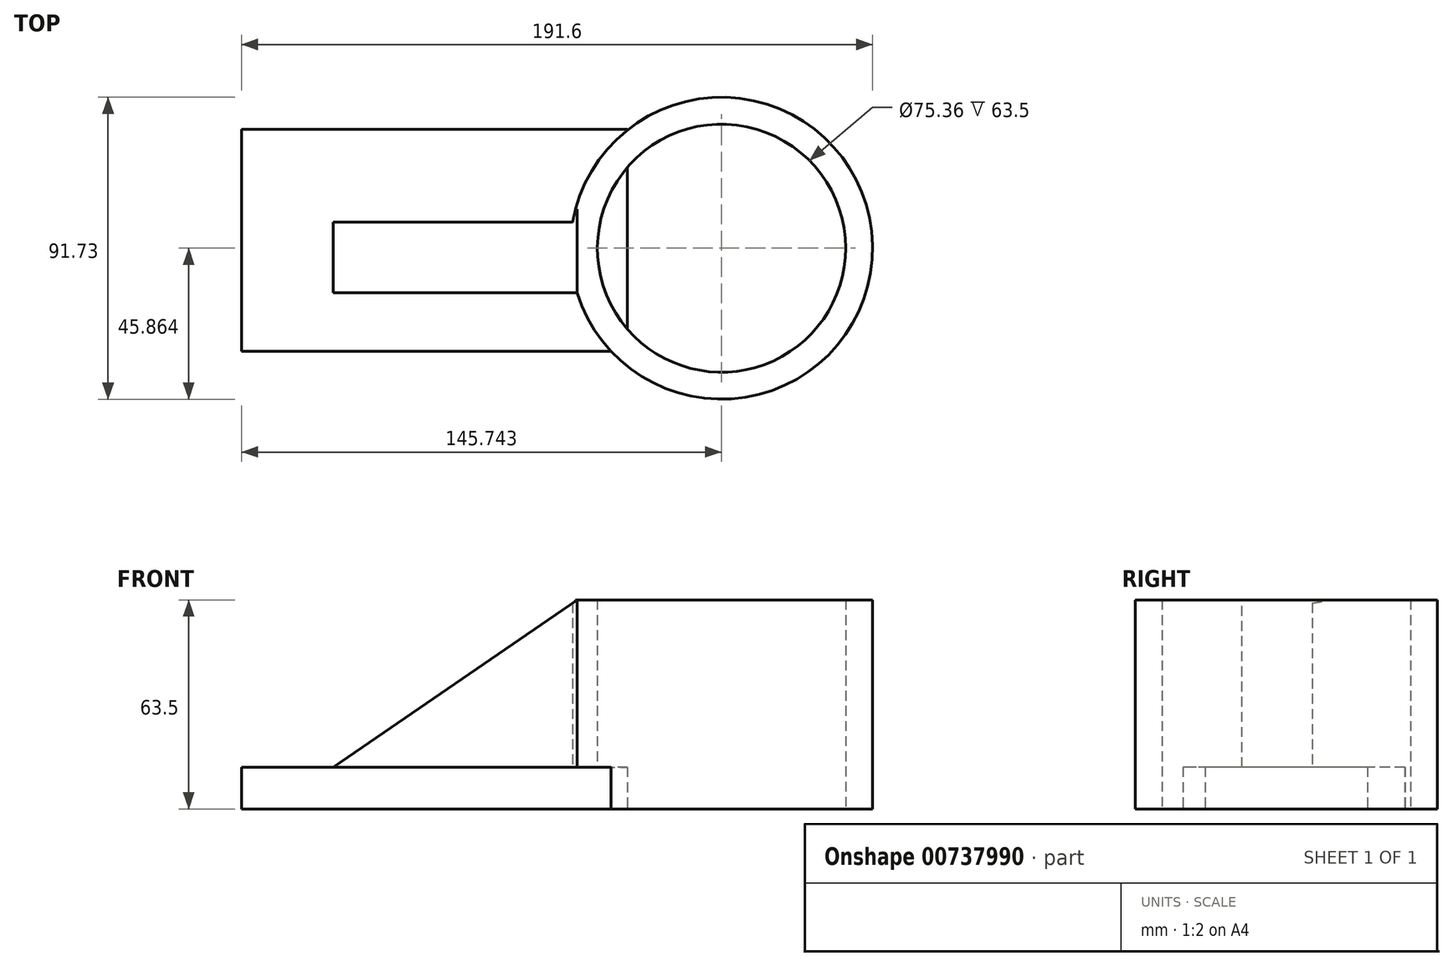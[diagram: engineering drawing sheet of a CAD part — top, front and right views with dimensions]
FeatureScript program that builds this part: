
annotation { "Feature Type Name" : "Feature", "Feature Type Description" : "" }
export const myFeature = defineFeature(function(context is Context, id is Id, definition is map)
    precondition{}
    {
        {
            var Q0;
            Q0=qCreatedBy(makeId("Top.planeOp"),FACE);
            var sketch = newSketch(context, id + "F0", { "sketchPlane" : qUnion([Q0])});
            skLineSegment(sketch, "E0.bottom", {"start": v(-49.58, 28.21) * mm, "end": v(67.63, 28.21) * mm});
            skLineSegment(sketch, "E0.top", {"start": v(-49.58, -39.2) * mm, "end": v(67.63, -39.2) * mm});
            skLineSegment(sketch, "E0.left", {"start": v(-49.58, 28.21) * mm, "end": v(-49.58, -39.2) * mm});
            skLineSegment(sketch, "E0.right", {"start": v(67.63, 28.21) * mm, "end": v(67.63, -39.2) * mm});
            skSolve(sketch);
        }
        {
            var Q0;
            Q0 = qSketchRegion(id + "F0", true);
            extrude(context, id + "F1", {"entities" : qUnion([Q0]), "depth" : 25.4 * mm, "offsetDistance" : 25.4 * mm});
        }
        {
            var Q0;
            Q0=makeQuery(id+"F1.opExtrude","CAP_FACE",FACE,{"disambiguationData":[OSD([sQuery(id+"F0.wireOp",EDGE,"E0.bottom"),sQuery(id+"F0.wireOp",EDGE,"E0.top"),sQuery(id+"F0.wireOp",EDGE,"E0.left"),sQuery(id+"F0.wireOp",EDGE,"E0.right")])],"isStart":false});
            extrude(context, id + "F2", {"entities" : qUnion([Q0]), "operationType" : NewBodyOperationType.REMOVE, "oppositeDirection" : true, "depth" : 12.7 * mm, "offsetDistance" : 25.4 * mm});
        }
        {
            var Q0;
            Q0=qCreatedBy(makeId("Top.planeOp"),FACE);
            var sketch = newSketch(context, id + "F3", { "sketchPlane" : qUnion([Q0])});
            skCircle(sketch, "E1", {"center": v(96.16, -7.88) * mm, "radius": 45.86 * mm});
            skCircle(sketch, "E2", {"center": v(96.16, -7.88) * mm, "radius": 37.68 * mm});
            skSolve(sketch);
        }
        {
            var Q0;
            Q0=makeQuery(id+"F3.imprint","IMPRINT",FACE,{"disambiguationData":[TD([[makeQuery(id+"F3.imprint","IMPRINT",EDGE,{"derivedFrom":sQuery(id+"F3.wireOp",EDGE,"E1")}),1.0]])]});
            var Q1;
            Q1 = qSketchRegion(id + "F3", true);
            extrude(context, id + "F4", {"entities" : qUnion([Q0, Q1]), "operationType" : NewBodyOperationType.ADD, "depth" : 63.5 * mm, "offsetDistance" : 25.4 * mm});
        }
        {
            var Q0;
            {var subQ0=sQuery(id+"F0.wireOp",EDGE,"E0.left");var subQ1=sQuery(id+"F0.wireOp",EDGE,"E0.top");var subQ2=sQuery(id+"F0.wireOp",EDGE,"E0.right");var subQ3=sQuery(id+"F0.wireOp",EDGE,"E0.bottom");Q0=makeQuery(id+"F4.boolean.opBoolean","SPLIT",FACE,{"disambiguationData":[TD([makeQuery(id+"F1.opExtrude","SWEPT_FACE",FACE,{"disambiguationData":[OSD([subQ3])]})])],"derivedFrom":makeQuery(id+"F2.boolean.opBoolean","COPY",FACE,{"derivedFrom":makeQuery(id+"F2.opExtrude","CAP_FACE",FACE,{"disambiguationData":[OSD([subQ3,subQ1,subQ0,subQ2])],"isStart":false})})});}
            var sketch = newSketch(context, id + "F5", { "sketchPlane" : qUnion([Q0])});
            skLineSegment(sketch, "E3.bottom", {"start": v(-21.7, 0) * mm, "end": v(52.33, 0) * mm});
            skLineSegment(sketch, "E3.top", {"start": v(-21.7, -21.37) * mm, "end": v(52.33, -21.37) * mm});
            skLineSegment(sketch, "E3.left", {"start": v(-21.7, 0) * mm, "end": v(-21.7, -21.37) * mm});
            skLineSegment(sketch, "E3.right", {"start": v(52.33, 0) * mm, "end": v(52.33, -21.37) * mm});
            skSolve(sketch);
        }
        {
            var Q0;
            Q0 = qSketchRegion(id + "F5", true);
            var Q1;
            {var subQ4=sQuery(id+"F5.wireOp",EDGE,"E3.top");Q1=makeQuery(id+"F5.imprint","IMPRINT",FACE,{"disambiguationData":[TD([[makeQuery(id+"F5.imprint","IMPRINT",EDGE,{"derivedFrom":subQ4}),1.0]])]});}
            extrude(context, id + "F6", {"entities" : qUnion([Q0, Q1]), "operationType" : NewBodyOperationType.ADD, "depth" : 50.8 * mm, "offsetDistance" : 25.4 * mm});
        }
        {
            var Q0;
            Q0=makeQuery(id+"F6.opExtrude","SWEPT_FACE",FACE,{"disambiguationData":[OSD([sQuery(id+"F5.wireOp",EDGE,"E3.top")])]});
            var sketch = newSketch(context, id + "F7", { "sketchPlane" : qUnion([Q0])});
            skLineSegment(sketch, "E4", {"start": v(-21.7, 12.7) * mm, "end": v(52.33, 63.5) * mm});
            skSolve(sketch);
        }
        {
            var Q0;
            Q0=makeQuery(id+"F7.imprint","IMPRINT",FACE,{"disambiguationData":[TD([[makeQuery(id+"F7.imprint","IMPRINT",EDGE,{"derivedFrom":sQuery(id+"F7.wireOp",EDGE,"E4")}),1.0]])]});
            extrude(context, id + "F8", {"entities" : qUnion([Q0]), "operationType" : NewBodyOperationType.REMOVE, "oppositeDirection" : true, "depth" : 25.4 * mm, "offsetDistance" : 25.4 * mm});
        }
    });
